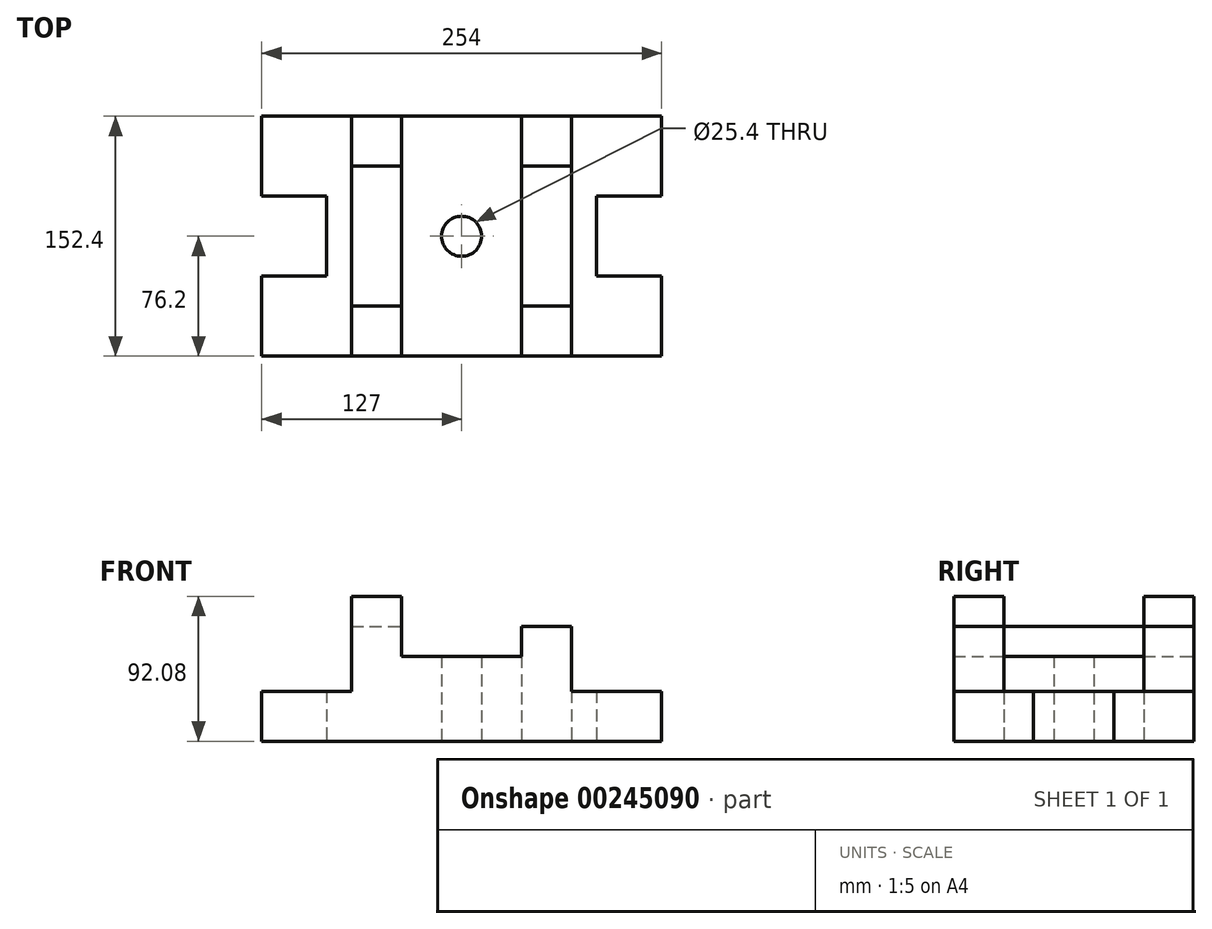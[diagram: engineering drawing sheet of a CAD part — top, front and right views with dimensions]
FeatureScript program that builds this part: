
annotation { "Feature Type Name" : "Feature", "Feature Type Description" : "" }
export const myFeature = defineFeature(function(context is Context, id is Id, definition is map)
    precondition{}
    {
        {
            var Q0;
            Q0=qCreatedBy(makeId("Top.planeOp"),FACE);
            var sketch = newSketch(context, id + "F0", { "sketchPlane" : qUnion([Q0])});
            skCircle(sketch, "E0", {"center": v(0, 0) * mm, "radius": 12.7 * mm});
            skLineSegment(sketch, "E1", {"start": v(0, 0) * mm, "end": v(0, -76.2) * mm});
            skLineSegment(sketch, "E2", {"start": v(0, -76.2) * mm, "end": v(-127, -76.2) * mm});
            skLineSegment(sketch, "E3", {"start": v(0, -76.2) * mm, "end": v(127, -76.2) * mm});
            skLineSegment(sketch, "E4", {"start": v(0, 0) * mm, "end": v(0, 76.2) * mm});
            skLineSegment(sketch, "E5", {"start": v(-127, 76.2) * mm, "end": v(0, 76.2) * mm});
            skLineSegment(sketch, "E6", {"start": v(0, 76.2) * mm, "end": v(127, 76.2) * mm});
            skLineSegment(sketch, "E7", {"start": v(-127, 76.2) * mm, "end": v(-127, 25.4) * mm});
            skLineSegment(sketch, "E8", {"start": v(-127, -25.4) * mm, "end": v(-127, -76.2) * mm});
            skLineSegment(sketch, "E9", {"start": v(-85.72, 25.4) * mm, "end": v(-127, 25.4) * mm});
            skLineSegment(sketch, "E10", {"start": v(-127, -25.4) * mm, "end": v(-85.72, -25.4) * mm});
            skLineSegment(sketch, "E11", {"start": v(-85.72, -25.4) * mm, "end": v(-85.72, 25.4) * mm});
            skLineSegment(sketch, "E12", {"start": v(127, 76.2) * mm, "end": v(127, 25.4) * mm});
            skLineSegment(sketch, "E13", {"start": v(127, 25.4) * mm, "end": v(127, 23.32) * mm});
            skLineSegment(sketch, "E14", {"start": v(127, 25.4) * mm, "end": v(85.73, 25.4) * mm});
            skLineSegment(sketch, "E15", {"start": v(85.73, -25.4) * mm, "end": v(85.73, 25.4) * mm});
            skLineSegment(sketch, "E16", {"start": v(85.73, -25.4) * mm, "end": v(127, -25.4) * mm});
            skLineSegment(sketch, "E17", {"start": v(127, -25.4) * mm, "end": v(127, -76.2) * mm});
            skLineSegment(sketch, "E18", {"start": v(85.73, 25.4) * mm, "end": v(69.85, 25.4) * mm});
            skLineSegment(sketch, "E19", {"start": v(69.85, 76.2) * mm, "end": v(69.85, -76.2) * mm});
            skLineSegment(sketch, "E20", {"start": v(69.85, 76.2) * mm, "end": v(38.1, 76.2) * mm});
            skLineSegment(sketch, "E21", {"start": v(38.1, -76.2) * mm, "end": v(38.1, 76.2) * mm});
            skLineSegment(sketch, "E22", {"start": v(38.1, 76.2) * mm, "end": v(38.1, 44.45) * mm});
            skLineSegment(sketch, "E23", {"start": v(69.85, 44.45) * mm, "end": v(38.1, 44.45) * mm});
            skLineSegment(sketch, "E24", {"start": v(69.85, 44.45) * mm, "end": v(69.85, 76.2) * mm});
            skLineSegment(sketch, "E25", {"start": v(38.1, 44.45) * mm, "end": v(38.1, 76.2) * mm});
            skLineSegment(sketch, "E26", {"start": v(38.1, 76.2) * mm, "end": v(69.85, 76.2) * mm});
            skLineSegment(sketch, "E27", {"start": v(38.1, 44.45) * mm, "end": v(69.85, 44.45) * mm});
            skLineSegment(sketch, "E28", {"start": v(69.85, -76.2) * mm, "end": v(69.85, -44.45) * mm});
            skLineSegment(sketch, "E29", {"start": v(69.85, -44.45) * mm, "end": v(38.1, -44.45) * mm});
            skLineSegment(sketch, "E30", {"start": v(38.1, -44.45) * mm, "end": v(38.1, -76.2) * mm});
            skLineSegment(sketch, "E31", {"start": v(38.1, -76.2) * mm, "end": v(69.85, -76.2) * mm});
            skLineSegment(sketch, "E32", {"start": v(0, 76.2) * mm, "end": v(0, -76.2) * mm});
            skLineSegment(sketch, "E33.MirrorCS", {"start": v(-38.1, 76.2) * mm, "end": v(-38.1, 44.45) * mm});
            skLineSegment(sketch, "E34.MirrorCS", {"start": v(-69.85, 44.45) * mm, "end": v(-38.1, 44.45) * mm});
            skLineSegment(sketch, "E35.MirrorCS", {"start": v(-69.85, 44.45) * mm, "end": v(-69.85, 76.2) * mm});
            skLineSegment(sketch, "E36.MirrorCS", {"start": v(-69.85, 76.2) * mm, "end": v(-38.1, 76.2) * mm});
            skLineSegment(sketch, "E37.MirrorCS", {"start": v(-69.85, 76.2) * mm, "end": v(-69.85, -76.2) * mm});
            skLineSegment(sketch, "E38.MirrorCS", {"start": v(-69.85, -44.45) * mm, "end": v(-38.1, -44.45) * mm});
            skLineSegment(sketch, "E39.MirrorCS", {"start": v(-69.85, -76.2) * mm, "end": v(-69.85, -44.45) * mm});
            skLineSegment(sketch, "E40.MirrorCS", {"start": v(-38.1, -76.2) * mm, "end": v(-69.85, -76.2) * mm});
            skLineSegment(sketch, "E41.MirrorCS", {"start": v(-38.1, -44.45) * mm, "end": v(-38.1, -76.2) * mm});
            skLineSegment(sketch, "E42.MirrorCS", {"start": v(-38.1, -76.2) * mm, "end": v(-38.1, 76.2) * mm});
            skLineSegment(sketch, "E43", {"start": v(-85.72, 25.4) * mm, "end": v(-85.72, 76.2) * mm});
            skLineSegment(sketch, "E44", {"start": v(-85.72, -25.4) * mm, "end": v(-85.72, -76.2) * mm});
            skLineSegment(sketch, "E45", {"start": v(85.73, 25.4) * mm, "end": v(85.73, 76.2) * mm});
            skLineSegment(sketch, "E46", {"start": v(85.73, -25.4) * mm, "end": v(85.73, -76.2) * mm});
            skSolve(sketch);
        }
        {
            var Q0;
            {var subQ0=sQuery(id+"F0.wireOp",EDGE,"E7");Q0=makeQuery(id+"F0.imprint","IMPRINT",FACE,{"disambiguationData":[TD([[makeQuery(id+"F0.imprint","IMPRINT",EDGE,{"derivedFrom":subQ0}),1.0]])]});}
            var Q1;
            {var subQ0=sQuery(id+"F0.wireOp",EDGE,"E8");Q1=makeQuery(id+"F0.imprint","IMPRINT",FACE,{"disambiguationData":[TD([[makeQuery(id+"F0.imprint","IMPRINT",EDGE,{"derivedFrom":subQ0}),1.0]])]});}
            var Q2;
            {var subQ0=sQuery(id+"F0.wireOp",EDGE,"E12");Q2=makeQuery(id+"F0.imprint","IMPRINT",FACE,{"disambiguationData":[TD([[makeQuery(id+"F0.imprint","IMPRINT",EDGE,{"derivedFrom":subQ0}),-1.0]])]});}
            var Q3;
            Q3=makeQuery(id+"F0.imprint","IMPRINT",FACE,{"disambiguationData":[TD([[makeQuery(id+"F0.imprint","IMPRINT",EDGE,{"derivedFrom":sQuery(id+"F0.wireOp",EDGE,"E16")}),-1.0]])]});
            var Q4;
            Q4=makeQuery(id+"F0.imprint","IMPRINT",FACE,{"disambiguationData":[TD([[makeQuery(id+"F0.imprint","IMPRINT",EDGE,{"derivedFrom":sQuery(id+"F0.wireOp",EDGE,"E15")}),1.0]])]});
            var Q5;
            {var subQ1=sQuery(id+"F0.wireOp",EDGE,"E18");Q5=makeQuery(id+"F0.imprint","IMPRINT",FACE,{"disambiguationData":[TD([[makeQuery(id+"F0.imprint","IMPRINT",EDGE,{"derivedFrom":subQ1}),-1.0]])]});}
            var Q6;
            Q6=makeQuery(id+"F0.imprint","IMPRINT",FACE,{"disambiguationData":[TD([[makeQuery(id+"F0.imprint","IMPRINT",EDGE,{"derivedFrom":sQuery(id+"F0.wireOp",EDGE,"E11")}),-1.0]])]});
            extrude(context, id + "F1", {"entities" : qUnion([Q0, Q1, Q2, Q3, Q4, Q5, Q6]), "depth" : 31.75 * mm});
        }
        {
            var Q0;
            {var subQ0=sQuery(id+"F0.wireOp",EDGE,"E34.MirrorCS");Q0=makeQuery(id+"F0.imprint","IMPRINT",FACE,{"disambiguationData":[TD([[makeQuery(id+"F0.imprint","IMPRINT",EDGE,{"derivedFrom":subQ0}),1.0]])]});}
            var Q1;
            {var subQ0=sQuery(id+"F0.wireOp",EDGE,"E38.MirrorCS");Q1=makeQuery(id+"F0.imprint","IMPRINT",FACE,{"disambiguationData":[TD([[makeQuery(id+"F0.imprint","IMPRINT",EDGE,{"derivedFrom":subQ0}),-1.0]])]});}
            var Q2;
            Q2=makeQuery(id+"F0.imprint","IMPRINT",FACE,{"disambiguationData":[TD([[makeQuery(id+"F0.imprint","IMPRINT",EDGE,{"derivedFrom":sQuery(id+"F0.wireOp",EDGE,"E24")}),1.0]])]});
            var Q3;
            Q3=makeQuery(id+"F0.imprint","IMPRINT",FACE,{"disambiguationData":[TD([[makeQuery(id+"F0.imprint","IMPRINT",EDGE,{"derivedFrom":sQuery(id+"F0.wireOp",EDGE,"E28")}),1.0]])]});
            extrude(context, id + "F2", {"entities" : qUnion([Q0, Q1, Q2, Q3]), "depth" : 92.07 * mm});
        }
        {
            var Q0;
            Q0=makeQuery(id+"F0.imprint","IMPRINT",FACE,{"disambiguationData":[TD([[makeQuery(id+"F0.imprint","IMPRINT",EDGE,{"derivedFrom":sQuery(id+"F0.wireOp",EDGE,"E21")}),-1.0]])]});
            var Q1;
            {var subQ0=sQuery(id+"F0.wireOp",EDGE,"E34.MirrorCS");Q1=makeQuery(id+"F0.imprint","IMPRINT",FACE,{"disambiguationData":[TD([[makeQuery(id+"F0.imprint","IMPRINT",EDGE,{"derivedFrom":subQ0}),-1.0]])]});}
            extrude(context, id + "F3", {"entities" : qUnion([Q0, Q1]), "operationType" : NewBodyOperationType.ADD, "depth" : 73.02 * mm});
        }
        {
            var Q0;
            {var subQ0=sQuery(id+"F0.wireOp",EDGE,"E32");var subQ3=sQuery(id+"F0.wireOp",EDGE,"E0");var subQ4=makeQuery(id+"F0.imprint","INTERSECT",VERTEX,{"disambiguationData":[OD(0.0)],"derivedFrom":[subQ3,subQ0]});Q0=makeQuery(id+"F0.imprint","IMPRINT",FACE,{"disambiguationData":[TD([[makeQuery(id+"F0.imprint","IMPRINT",EDGE,{"disambiguationData":[TD([[subQ4,-1.0]])],"derivedFrom":subQ3}),-1.0]])]});}
            var Q1;
            Q1=makeQuery(id+"F0.imprint","IMPRINT",FACE,{"disambiguationData":[TD([[makeQuery(id+"F0.imprint","IMPRINT",EDGE,{"derivedFrom":sQuery(id+"F0.wireOp",EDGE,"E21")}),1.0]])]});
            extrude(context, id + "F4", {"entities" : qUnion([Q0, Q1]), "operationType" : NewBodyOperationType.ADD, "depth" : 53.97 * mm});
        }
    });
